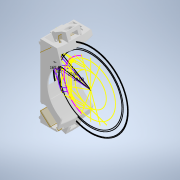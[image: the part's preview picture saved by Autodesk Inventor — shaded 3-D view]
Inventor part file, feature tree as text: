
AUTODESK INVENTOR PART (.ipt)
format: ipt  version: 2022 (Build 260153000, 153)  size: 3,268,608 bytes
history: native  units: mm
features: reference x91, projected_geometry x43, other x33, sketch x33, extrude x32, fillet x20, mirror x13, chamfer x5, revolve x3
ambient origin geometry x8: Origin, YZ Plane, XZ Plane, XY Plane, X Axis, Y Axis, Z Axis, Center Point
bodies: Body1 (feature_tree)
feature tree (273):
  other  "Твердое тело1"
  sketch  "Эскиз1"
  extrude  "Выдавливание1"  Depth=3.490659mm
  extrude  "Выдавливание2"  Depth=3.490659mm
  extrude  "Выдавливание3"  Depth=1.0mm
  sketch  "Эскиз5"
  extrude  "Выдавливание4"  Depth=1.0mm
  extrude  "Выдавливание5"  Depth=4.537856mm
  other  "РабПлоскость1"
  extrude  "Выдавливание6"  Depth=4.537856mm
  extrude  "Выдавливание7"  Depth=0.5mm
  extrude  "Выдавливание8"  Depth=18.69mm TaperAngle=0.0deg
  fillet  "Сопряжение2"  Radius=20.45mm
  extrude  "Выдавливание9"  Depth=1.5mm TaperAngle=0.0deg
  extrude  "Выдавливание10"  Depth=1.5mm
  fillet  "Сопряжение3"  Radius=3.0mm
  fillet  "Сопряжение4"  [1 undecoded]
  extrude  "Выдавливание11"  Depth=9.162979mm
  fillet  "Сопряжение6"  Radius=2.0mm
  fillet  "Сопряжение7"  Radius=28.843311mm
  extrude  "Выдавливание12"  Depth=1.5mm
  extrude  "Выдавливание13"  Depth=1.2mm
  fillet  "Сопряжение8"  Radius=20.69mm
  revolve  "Вращение1"
  fillet  "Сопряжение9"  Radius=11.0mm
  fillet  "Сопряжение10"  Radius=1.3mm
  extrude  "Выдавливание14"  Depth=14.5mm
  fillet  "Сопряжение11"  Radius=11.0mm
  fillet  "Сопряжение12"  Radius=9.0mm
  fillet  "Сопряжение13"  Radius=9.0mm
  chamfer  "Фаска1"  Distance=2.0mm
  extrude  "Выдавливание15"  Depth=1.0mm
  fillet  "Сопряжение14"  Radius=0.3mm
  extrude  "Выдавливание16"  Depth=0.3mm
  extrude  "Выдавливание17"  Depth=0.3mm
  revolve  "Вращение2"
  extrude  "Выдавливание18"  Depth=0.3mm
  mirror  "Зеркальное отражение2"
  other  "РабПлоскость4"
  extrude  "Выдавливание19"  Depth=25.0mm TaperAngle=0.0deg
  extrude  "Выдавливание20"  Depth=0.3mm TaperAngle=0.0deg
  mirror  "Зеркальное отражение3"
  mirror  "Зеркальное отражение4"
  fillet  "Сопряжение18"  Radius=2.0mm
  extrude  "Выдавливание21"  Depth=10.0mm TaperAngle=0.0deg
  mirror  "Зеркальное отражение5"
  extrude  "Выдавливание22"  Depth=1.0mm
  mirror  "Зеркальное отражение6"
  extrude  "Выдавливание23"  Depth=0.7mm
  other  "РабПлоскость2"
  extrude  "Выдавливание24"  Depth=0.7mm
  extrude  "Выдавливание25"  Depth=0.3mm
  fillet  "Сопряжение20"  Radius=0.2mm
  fillet  "Сопряжение21"  Radius=0.2mm
  mirror  "Зеркальное отражение7"
  extrude  "Выдавливание26"  Depth=0.5mm
  mirror  "Зеркальное отражение8"
  mirror  "Зеркальное отражение9"
  revolve  "Вращение4"
  fillet  "Сопряжение26"  Radius=3.5mm
  fillet  "Сопряжение27"  Radius=0.8mm
  extrude  "Выдавливание27"  Depth=2.0mm
  mirror  "Зеркальное отражение10"
  extrude  "Выдавливание28"  Depth=2.0mm
  chamfer  "Фаска3"  Distance=200.0mm
  fillet  "Сопряжение28"  Radius=0.5mm
  extrude  "Выдавливание29"  Depth=0.5mm
  chamfer  "Фаска4"  Distance=2.0mm
  fillet  "Сопряжение29"  Radius=2.0mm
  mirror  "Зеркальное отражение11"
  mirror  "Зеркальное отражение12"
  extrude  "Выдавливание30"  Depth=0.5mm
  mirror  "Зеркальное отражение13"
  fillet  "Сопряжение30"  Radius=3.490659mm
  chamfer  "Фаска5"  Distance=2.0mm
  extrude  "Выдавливание31"  TaperAngle=360.0deg  [1 undecoded]
  extrude  "Выдавливание32"  Depth=0.7mm
  chamfer  "Фаска6"  Distance=2.0mm
  other  "РабПлоскость5"
  mirror  "Зеркальное отражение14"
  reference  "Ссылка1"
  reference  "Ссылка2"
  reference  "Ссылка3"
  reference  "Ссылка4"
  reference  "Ссылка5"
  reference  "Ссылка6"
  reference  "Ссылка7"
  reference  "Ссылка8"
  reference  "Ссылка9"
  reference  "Ссылка10"
  reference  "Ссылка11"
  reference  "Ссылка12"
  reference  "Ссылка13"
  reference  "Ссылка14"
  reference  "Ссылка15"
  reference  "Ссылка16"
  reference  "Ссылка17"
  reference  "Ссылка18"
  reference  "Ссылка19"
  reference  "Ссылка20"
  reference  "Ссылка21"
  reference  "Ссылка22"
  reference  "Ссылка23"
  reference  "Ссылка24"
  reference  "Ссылка25"
  sketch  "Эскиз2"
  reference  "Ссылка26"
  reference  "Ссылка27"
  reference  "Ссылка28"
  reference  "Ссылка29"
  reference  "Ссылка30"
  sketch  "Эскиз3"
  projected_geometry  "Спроецированная петля1"
  projected_geometry  "Спроецированная петля2"
  reference  "Ссылка31"
  sketch  "Эскиз4"
  projected_geometry  "Спроецированная петля3"
  reference  "Ссылка32"
  projected_geometry  "Спроецированная петля4"
  projected_geometry  "Спроецированная петля5"
  reference  "Ссылка33"
  reference  "Ссылка34"
  reference  "Ссылка35"
  reference  "Ссылка47"
  sketch  "Эскиз6"
  projected_geometry  "Спроецированная петля6"
  sketch  "Эскиз7"
  projected_geometry  "Спроецированная петля7"
  sketch  "Эскиз8"
  reference  "Ссылка51"
  projected_geometry  "Спроецированная петля8"
  sketch  "Эскиз10"
  reference  "Ссылка54"
  reference  "Ссылка55"
  reference  "Ссылка56"
  reference  "Ссылка57"
  reference  "Ссылка58"
  sketch  "Эскиз11"
  projected_geometry  "Спроецированная петля9"
  sketch  "Эскиз12"
  projected_geometry  "Спроецированная петля10"
  reference  "Ссылка59"
  reference  "Ссылка60"
  reference  "Ссылка61"
  sketch  "Эскиз13"
  reference  "Ссылка62"
  reference  "Ссылка63"
  reference  "Ссылка64"
  reference  "Ссылка65"
  sketch  "Эскиз14"
  reference  "Ссылка66"
  projected_geometry  "Спроецированная петля11"
  sketch  "Эскиз15"
  projected_geometry  "Спроецированная петля12"
  sketch  "Эскиз16"
  reference  "Ссылка67"
  reference  "Ссылка68"
  reference  "Ссылка69"
  reference  "Ссылка70"
  reference  "Ссылка71"
  reference  "Ссылка72"
  sketch  "Эскиз17"
  reference  "Ссылка73"
  reference  "Ссылка74"
  projected_geometry  "Спроецированная петля13"
  projected_geometry  "Спроецированная петля14"
  reference  "Ссылка75"
  reference  "Ссылка76"
  sketch  "Эскиз18"
  reference  "Ссылка77"
  reference  "Ссылка78"
  reference  "Ссылка79"
  reference  "Ссылка80"
  reference  "Ссылка81"
  reference  "Ссылка82"
  reference  "Ссылка83"
  reference  "Ссылка84"
  sketch  "Эскиз19"
  projected_geometry  "Спроецированная петля15"
  projected_geometry  "Спроецированная петля16"
  projected_geometry  "Спроецированная петля17"
  sketch  "Эскиз20"
  sketch  "Эскиз21"
  sketch  "Эскиз22"
  projected_geometry  "Спроецированная петля19"
  sketch  "Эскиз24"
  projected_geometry  "Спроецированная петля20"
  projected_geometry  "Спроецированная петля23"
  reference  "Ссылка95"
  reference  "Ссылка96"
  reference  "Ссылка97"
  projected_geometry  "Спроецированная петля24"
  projected_geometry  "Спроецированная петля25"
  projected_geometry  "Спроецированная петля26"
  projected_geometry  "Спроецированная петля27"
  projected_geometry  "Спроецированная петля28"
  projected_geometry  "Спроецированная петля29"
  projected_geometry  "Спроецированная петля30"
  reference  "Ссылка103"
  reference  "Ссылка104"
  reference  "Ссылка105"
  reference  "Ссылка106"
  sketch  "Эскиз27"
  reference  "Ссылка107"
  projected_geometry  "Спроецированная петля31"
  projected_geometry  "Спроецированная петля32"
  reference  "Ссылка108"
  reference  "Ссылка109"
  reference  "Ссылка110"
  sketch  "Эскиз28"
  reference  "Ссылка111"
  projected_geometry  "Спроецированная петля33"
  sketch  "Эскиз29"
  reference  "Ссылка112"
  sketch  "Эскиз30"
  projected_geometry  "Спроецированная петля34"
  other  "РабПлоскость3"
  reference  "Ссылка113"
  projected_geometry  "Спроецированная петля35"
  sketch  "Эскиз32"
  projected_geometry  "Спроецированная петля37"
  projected_geometry  "Спроецированная петля38"
  sketch  "Эскиз33"
  sketch  "Эскиз34"
  projected_geometry  "Спроецированная петля39"
  projected_geometry  "Спроецированная петля40"
  projected_geometry  "Спроецированная петля41"
  projected_geometry  "Спроецированная петля42"
  projected_geometry  "Спроецированная петля43"
  sketch  "Эскиз36"
  projected_geometry  "Спроецированная петля44"
  reference  "Ссылка114"
  reference  "Ссылка115"
  reference  "Ссылка116"
  sketch  "Эскиз37"
  projected_geometry  "Спроецированная петля45"
  reference  "Ссылка117"
  reference  "Ссылка118"
  reference  "Ссылка119"
  reference  "Ссылка120"
  reference  "Ссылка121"
  reference  "Ссылка122"
  sketch  "Эскиз38"
  sketch  "Эскиз39"
  projected_geometry  "Спроецированная петля46"
  projected_geometry  "Спроецированная петля47"
  other  "РабПлоскость6"
  other  "<userpath>\Documents\Git\MZCAT_2024\MZCAT_2.iam"
  other  "MZCAT_2.iam"
  other  "lidar_krestovina:1"
  other  "shatun_lidar:1"
  other  "stabilisator_plan:1"
  other  "OCS-D008 B:3"
  other  "commutationCATboard:1"
  other  "CAT_protector:1"
  other  "OCS-D008 B:2"
  other  "<userpath>\Documents\Git\MZCAT_2024_construction\MZCAT_2024_RPI\MZCAT_4.iam"
  other  "MZCAT_4.iam"
  other  "vydacha_pusher:2"
  other  "FastBattery:1"
  other  "metal_cap:1"
  other  "base plate:1"
  other  "base plate:2"
  other  "<userpath>\Documents\Git\MZCAT_2024\MZCAT_3.iam"
  other  "MZCAT_3.iam"
  other  "akkum_cup:1"
  other  "vydacha_slide:1"
  other  "<userpath>\Documents\Git\MZCAT_2024\MZCAT_4.iam"
  other  "ov13855:1"
  other  "shelka_lidar:1"
  other  "shelka_lidar:2"
  other  "ov13855:2"
  other  "<userpath>\Documents\Git\MZCAT_2024\MZCAT_4.iam"
note: 2 required parameter values undecoded (feature->parameter linkage not recoverable at this tier; creation-order binding heuristic only, values carry confidence <= 0.55)
